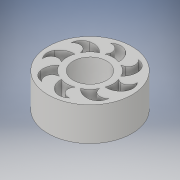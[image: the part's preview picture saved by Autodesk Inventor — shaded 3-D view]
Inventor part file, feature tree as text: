
AUTODESK INVENTOR PART (.ipt)
format: ipt  version: 2018 (Build 220112000, 112)  size: 179,200 bytes
history: native  units: in
note: dims shown in document units (in); Inventor stores cm internally (conversion verified against a paired STEP export)
features: extrude x2, sketch x2, pattern_circular x1
ambient origin geometry x8: Origin, YZ Plane, XZ Plane, XY Plane, X Axis, Y Axis, Z Axis, Center Point
bodies: Solid1 (feature_tree)
feature tree (5):
  extrude  "Extrusion1"  Depth=1.0in
  extrude  "Extrusion2"  Depth=1.0in
  pattern_circular  "Circular Pattern1"  [2 undecoded]
  sketch  "Sketch1"  dims[d0=1.0in d1=2.5in]
  sketch  "Sketch2"  dims[d2=1.0in d3=0.0in d4=0.2in d6=0.2in d7=0.4in d8=1.0in d9=0.0in d10=3.1496in d11=360.0deg d13=0.4in]
note: 2 required parameter values undecoded (feature->parameter linkage not recoverable at this tier; creation-order binding heuristic only, values carry confidence <= 0.55)
